# Revit family: VIESSMANN - Vitocal 350-HT Pro
name_source: partatom
category: Wyposażenie mechaniczne
revit_build: Autodesk Revit 2017 (Build: 20160720_1515(x64)
units: mm (PartAtom-declared; Revit-internal decimal feet)

## family parameters
Numer OmniClass = 23.75.10.21.17
Oparty na płaszczyźnie roboczej = Nie
Punkt obliczania pomieszczeń = Nie
Tnij formami wycięć po wczytaniu = Nie
Typ części = Normalny
Tytuł OmniClass = Water-Source Heat Pumps
Współdzielony = Nie
Wymiar okrągłego złącza = Użyj średnicy
Zawsze pionowo = Tak

## types (7) — shared parameters
Autor = www.archispace.pl
Czynnik chłodniczy = R1234ze
Częstotliwość = 50 Hz
Długość strefy serwisowej od przodu = 800 mm  [stored 2.62467 ft]
Liczba biegunów = 3
Maks. cos fi = 1 A
Model = Solankowa pompa ciepła Vitocal 350-HT PRO 80kW / Brine-water heat pump Vitocal 350-HT PRO 80kW
Napięcie znamionowe = 400 V
Obieg pierwotny. Maks. temperatura zasilania na wlocie obiegu pierwotnego = 50 °C
Obieg pierwotny. Min. temperatura zasilania na wlocie obiegu pierwotnego = 0 °C
Odsunięcie strefy serwisowej w szerokości = 456 mm
Opis = Pompy ciepła z napędem elektrycznym do ogrzewania i podgrzewu ciepłej wody użytkowej w jedno- lub dwusystemowych instalacjach grzewczych.
Podłączenie A odsunięcie = 731 mm  [stored 2.39829 ft]
Podłączenie A wysokość = 1365 mm  [stored 4.47835 ft]
Podłączenie C odsunięcie = 311 mm  [stored 1.02034 ft]
Podłączenie C wysokość = 509 mm  [stored 1.66995 ft]
Podłączenie D odsunięcie = 311 mm  [stored 1.02034 ft]
Podłączenie D wysokość = 969 mm  [stored 3.17913 ft]
Podłączenie E odsunięcie = 525 mm
Podłączenie E wysokość = 969 mm  [stored 3.17913 ft]
Podłączenie F odsunięcie = 525 mm
Podłączenie F wysokość = 509 mm  [stored 1.66995 ft]
Podłączenie elektryczne odsunięcie = 797 mm
Podłączenie elektryczne wysokość = 1566 mm
Producent = Viessmann Sp. z o.o.
Stopień ochrony = IP20
Szerokość całkowita = 911 mm  [stored 2.98885 ft]
Szerokość na wlocie = 850 mm  [stored 2.78871 ft]
URL = https://www.viessmann-projektant.pl
Viessmann Kolor 1 = Viessmann Kolor 1
Współczynnik mocy = 1
Wysokość całkowita = 1650 mm  [stored 5.41339 ft]
Zasilanie elektryczne (V/ph/Hz) = 3LNPE/400 V/50 Hz

## per-type parameters (varying)
- BW solanka-woda 2-stopniowy (B0/W35) 352.AHT058: Dopuszczalne ciśnienie robocze. Obieg pierwotny=10 pasek; Dopuszczalne ciśnienie robocze. Obieg wtórny=10 pasek; Dopuszczalne ciśnienie robocze. Strona niskociśnieniowa=19 pasek; Dopuszczalne ciśnienie robocze. Strona wysokociśnieniowa=32 pasek; Długość całkowita=2153 mm  [stored 7.06365 ft]; Ilość oleju=11.0 L; Liczba sprężarek=2; Maks. prąd roboczy=74 A; Masa całkowita (urządzenie podstawowe bez opcjonalnej obudowy)=1077.00 kg; Natężenie znamionowe sprężarek (łącznie)=34 A; Obciążenie pozorne=56600 W; Obieg pierwotny. Minimalny przepływ objętościowy=14.4 m³/h; Obieg pierwotny. Opory przepływu=26.1 pasek; Obieg pierwotny. Pojemność wymiennika ciepła (solanka)=13.0 L; Obieg pierwotny. Znamionowy przepływ objętościowy (wartość zalecana do projektowania)=20.3 m³/h; Obieg wtórny. Maks. temperatura na zasilaniu na wlocie obiegu pierwotnego = 0°=87 °C; Obieg wtórny. Min. temperatura na zasilaniu obiegu wtórnego=24 °C; Obieg wtórny. Minimalny przepływ objętościowy=8.5 m³/h; Obieg wtórny. Opory przepływu=7.7 pasek; Obieg wtórny. Pojemność wymiennika ciepła (woda)=13.0 L; Obieg wtórny. Znamionowy przepływ objętościowy (wartość zalecana do projektowania)=16.6 m³/h; Pobór mocy elektrycznej=13.2 kW; Poziom ciśnienia akustycznego dB(A)=60 mm  [stored 0.19685 ft]; Prąd rozruchowy sprężarki (Part Winding)=Po 125; Prąd rozruchowy sprężarki (łagodny rozruch)=Po 132; SCOP HT=3.11; SCOP LT=3.94; Stopień efektywności ε (COP)=4.3; Typ=Vitocal 350-HT Pro : BW 352.B076, BW 352.B097, BW 352.B114; Wielkość napełnienia (wytyczna)=22.50 kg; Wydajność chłodnicza=43.4 kW; Zabezpieczenie pompy ciepła=125 A; Zasilanie i powrót instalacji grzewczej - przyłącza Victaulic (DN)=65; Zasilanie i powrót obiegu pierwotnego - przyłącza Victaulic (DN)=65; Znamionowa moc grzewcza=56.6 kW; etas HT=117; etas LT=150
- BW solanka-woda 2-stopniowy (B0/W35) 352.AHT071: Dopuszczalne ciśnienie robocze. Obieg pierwotny=32 pasek; Dopuszczalne ciśnienie robocze. Obieg wtórny=19 pasek; Dopuszczalne ciśnienie robocze. Strona niskociśnieniowa=10 pasek; Dopuszczalne ciśnienie robocze. Strona wysokociśnieniowa=10 pasek; Długość całkowita=2153 mm  [stored 7.06365 ft]; Ilość oleju=11.0 L; Liczba sprężarek=2; Maks. prąd roboczy=100 A; Masa całkowita (urządzenie podstawowe bez opcjonalnej obudowy)=1077.00 kg; Natężenie znamionowe sprężarek (łącznie)=49 A; Obciążenie pozorne=72400 W; Obieg pierwotny. Minimalny przepływ objętościowy=14.4 m³/h; Obieg pierwotny. Opory przepływu=0.1 pasek; Obieg pierwotny. Pojemność wymiennika ciepła (solanka)=18.0 L; Obieg pierwotny. Znamionowy przepływ objętościowy (wartość zalecana do projektowania)=17.4 m³/h; Obieg wtórny. Maks. temperatura na zasilaniu na wlocie obiegu pierwotnego = 0°=73 °C; Obieg wtórny. Min. temperatura na zasilaniu obiegu wtórnego=20 °C; Obieg wtórny. Minimalny przepływ objętościowy=8.5 m³/h; Obieg wtórny. Opory przepływu=0.1 pasek; Obieg wtórny. Pojemność wymiennika ciepła (woda)=13.0 L; Obieg wtórny. Znamionowy przepływ objętościowy (wartość zalecana do projektowania)=13.4 m³/h; Pobór mocy elektrycznej=17.0 kW; Poziom ciśnienia akustycznego dB(A)=60 mm  [stored 0.19685 ft]; Prąd rozruchowy sprężarki (Part Winding)=Po 165; Prąd rozruchowy sprężarki (łagodny rozruch)=Po 160; SCOP HT=3.11; SCOP LT=3.94; Stopień efektywności ε (COP)=4.3; Typ=Vitocal 350-HT Pro : BW 352.B076, BW 352.B097, BW 352.B114; Wielkość napełnienia (wytyczna)=30.00 kg; Wydajność chłodnicza=55.4 kW; Zabezpieczenie pompy ciepła=125 A; Zasilanie i powrót instalacji grzewczej - przyłącza Victaulic (DN)=80; Zasilanie i powrót obiegu pierwotnego - przyłącza Victaulic (DN)=80; Znamionowa moc grzewcza=72.4 kW; etas HT=117; etas LT=150
- BW solanka-woda 2-stopniowy (B0/W35) 352.AHT084: Dopuszczalne ciśnienie robocze. Obieg pierwotny=10 pasek; Dopuszczalne ciśnienie robocze. Obieg wtórny=10 pasek; Dopuszczalne ciśnienie robocze. Strona niskociśnieniowa=19 pasek; Dopuszczalne ciśnienie robocze. Strona wysokociśnieniowa=32 pasek; Długość całkowita=2153 mm  [stored 7.06365 ft]; Ilość oleju=11.5 L; Liczba sprężarek=2; Maks. prąd roboczy=115 A; Masa całkowita (urządzenie podstawowe bez opcjonalnej obudowy)=1251.00 kg; Natężenie znamionowe sprężarek (łącznie)=51 A; Obciążenie pozorne=83200 W; Obieg pierwotny. Minimalny przepływ objętościowy=17.3 m³/h; Obieg pierwotny. Opory przepływu=14 pasek; Obieg pierwotny. Pojemność wymiennika ciepła (solanka)=22.0 L; Obieg pierwotny. Znamionowy przepływ objętościowy (wartość zalecana do projektowania)=20.0 m³/h; Obieg wtórny. Maks. temperatura na zasilaniu na wlocie obiegu pierwotnego = 0°=73 °C; Obieg wtórny. Min. temperatura na zasilaniu obiegu wtórnego=20 °C; Obieg wtórny. Minimalny przepływ objętościowy=10.0 m³/h; Obieg wtórny. Opory przepływu=13 pasek; Obieg wtórny. Pojemność wymiennika ciepła (woda)=15.0 L; Obieg wtórny. Znamionowy przepływ objętościowy (wartość zalecana do projektowania)=14.4 m³/h; Pobór mocy elektrycznej=19.6 kW; Poziom ciśnienia akustycznego dB(A)=65 mm  [stored 0.213255 ft]; Prąd rozruchowy sprężarki (Part Winding)=Po 165; Prąd rozruchowy sprężarki (łagodny rozruch)=Po 193; SCOP HT=3.21; SCOP LT=3.92; Stopień efektywności ε (COP)=4.2; Typ=Vitocal 350-HT Pro : BW 352.B076, BW 352.B097, BW 352.B114; Wielkość napełnienia (wytyczna)=36.00 kg; Wydajność chłodnicza=63.6 kW; Zabezpieczenie pompy ciepła=160 A; Zasilanie i powrót instalacji grzewczej - przyłącza Victaulic (DN)=80; Zasilanie i powrót obiegu pierwotnego - przyłącza Victaulic (DN)=80; Znamionowa moc grzewcza=83.2 kW; etas HT=120; etas LT=149
- BW solanka-woda 2-stopniowy (B0/W35) 352.AHT096: Dopuszczalne ciśnienie robocze. Obieg pierwotny=10 pasek; Dopuszczalne ciśnienie robocze. Obieg wtórny=10 pasek; Dopuszczalne ciśnienie robocze. Strona niskociśnieniowa=19 pasek; Dopuszczalne ciśnienie robocze. Strona wysokociśnieniowa=32 pasek; Długość całkowita=2153 mm  [stored 7.06365 ft]; Ilość oleju=11.5 L; Liczba sprężarek=2; Maks. prąd roboczy=136 A; Masa całkowita (urządzenie podstawowe bez opcjonalnej obudowy)=1357.00 kg; Natężenie znamionowe sprężarek (łącznie)=67 A; Obciążenie pozorne=96600 W; Obieg pierwotny. Minimalny przepływ objętościowy=15.4 m³/h; Obieg pierwotny. Opory przepływu=15 pasek; Obieg pierwotny. Pojemność wymiennika ciepła (solanka)=33.0 L; Obieg pierwotny. Znamionowy przepływ objętościowy (wartość zalecana do projektowania)=23.1 m³/h; Obieg wtórny. Maks. temperatura na zasilaniu na wlocie obiegu pierwotnego = 0°=73 °C; Obieg wtórny. Min. temperatura na zasilaniu obiegu wtórnego=20 °C; Obieg wtórny. Minimalny przepływ objętościowy=11.0 m³/h; Obieg wtórny. Opory przepływu=14 pasek; Obieg wtórny. Pojemność wymiennika ciepła (woda)=17.0 L; Obieg wtórny. Znamionowy przepływ objętościowy (wartość zalecana do projektowania)=16.7 m³/h; Pobór mocy elektrycznej=23.2 kW; Poziom ciśnienia akustycznego dB(A)=65 mm  [stored 0.213255 ft]; Prąd rozruchowy sprężarki (Part Winding)=Po 219; Prąd rozruchowy sprężarki (łagodny rozruch)=Po 222; SCOP HT=3.11; SCOP LT=3.86; Stopień efektywności ε (COP)=4.2; Typ=Vitocal 350-HT Pro : BW 352.B076, BW 352.B097, BW 352.B114; Wielkość napełnienia (wytyczna)=42.00 kg; Wydajność chłodnicza=73.4 kW; Zabezpieczenie pompy ciepła=160 A; Zasilanie i powrót instalacji grzewczej - przyłącza Victaulic (DN)=80; Zasilanie i powrót obiegu pierwotnego - przyłącza Victaulic (DN)=80; Znamionowa moc grzewcza=96.6 kW; etas HT=116; etas LT=146
- BW solanka-woda 2-stopniowy (B0/W35) 352.AHT119: Dopuszczalne ciśnienie robocze. Obieg pierwotny=10 pasek; Dopuszczalne ciśnienie robocze. Obieg wtórny=10 pasek; Dopuszczalne ciśnienie robocze. Strona niskociśnieniowa=19 pasek; Dopuszczalne ciśnienie robocze. Strona wysokociśnieniowa=32 pasek; Długość całkowita=2153 mm  [stored 7.06365 ft]; Ilość oleju=11.5 L; Liczba sprężarek=2; Maks. prąd roboczy=166 A; Masa całkowita (urządzenie podstawowe bez opcjonalnej obudowy)=1426.00 kg; Natężenie znamionowe sprężarek (łącznie)=91 A; Obciążenie pozorne=116800 W; Obieg pierwotny. Minimalny przepływ objętościowy=17.3 m³/h; Obieg pierwotny. Opory przepływu=16 pasek; Obieg pierwotny. Pojemność wymiennika ciepła (solanka)=39.0 L; Obieg pierwotny. Znamionowy przepływ objętościowy (wartość zalecana do projektowania)=27.8 m³/h; Obieg wtórny. Maks. temperatura na zasilaniu na wlocie obiegu pierwotnego = 0°=73 °C; Obieg wtórny. Min. temperatura na zasilaniu obiegu wtórnego=20 °C; Obieg wtórny. Minimalny przepływ objętościowy=13.0 m³/h; Obieg wtórny. Opory przepływu=17 pasek; Obieg wtórny. Pojemność wymiennika ciepła (woda)=20.0 L; Obieg wtórny. Znamionowy przepływ objętościowy (wartość zalecana do projektowania)=20.2 m³/h; Pobór mocy elektrycznej=28.4 kW; Poziom ciśnienia akustycznego dB(A)=65 mm  [stored 0.213255 ft]; Prąd rozruchowy sprężarki (Part Winding)=Po 226; Prąd rozruchowy sprężarki (łagodny rozruch)=Po 252; SCOP HT=3.07; SCOP LT=3.82; Stopień efektywności ε (COP)=4.1; Typ=Vitocal 350-HT Pro : BW 352.B076, BW 352.B097, BW 352.B114; Wielkość napełnienia (wytyczna)=49.50 kg; Wydajność chłodnicza=88.4 kW; Zabezpieczenie pompy ciepła=200 A; Zasilanie i powrót instalacji grzewczej - przyłącza Victaulic (DN)=80; Zasilanie i powrót obiegu pierwotnego - przyłącza Victaulic (DN)=80; Znamionowa moc grzewcza=116.8 kW; etas HT=115; etas LT=145
- BW solanka-woda 3-stopniowy (B0/W35) 352.AHT126: Dopuszczalne ciśnienie robocze. Obieg pierwotny=10 pasek; Dopuszczalne ciśnienie robocze. Obieg wtórny=10 pasek; Dopuszczalne ciśnienie robocze. Strona niskociśnieniowa=19 pasek; Dopuszczalne ciśnienie robocze. Strona wysokociśnieniowa=32 pasek; Długość całkowita=2816 mm  [stored 9.23885 ft]; Ilość oleju=16.3 L; Liczba sprężarek=3; Maks. prąd roboczy=173 A; Masa całkowita (urządzenie podstawowe bez opcjonalnej obudowy)=1779.00 kg; Natężenie znamionowe sprężarek (łącznie)=77 A; Obciążenie pozorne=124800 W; Obieg pierwotny. Minimalny przepływ objętościowy=19.2 m³/h; Obieg pierwotny. Opory przepływu=15 pasek; Obieg pierwotny. Pojemność wymiennika ciepła (solanka)=42.0 L; Obieg pierwotny. Znamionowy przepływ objętościowy (wartość zalecana do projektowania)=30.0 m³/h; Obieg wtórny. Maks. temperatura na zasilaniu na wlocie obiegu pierwotnego = 0°=73 °C; Obieg wtórny. Min. temperatura na zasilaniu obiegu wtórnego=20 °C; Obieg wtórny. Minimalny przepływ objętościowy=15.5 m³/h; Obieg wtórny. Opory przepływu=16 pasek; Obieg wtórny. Pojemność wymiennika ciepła (woda)=23.0 L; Obieg wtórny. Znamionowy przepływ objętościowy (wartość zalecana do projektowania)=21.6 m³/h; Pobór mocy elektrycznej=29.4 kW; Poziom ciśnienia akustycznego dB(A)=65 mm  [stored 0.213255 ft]; Prąd rozruchowy sprężarki (Part Winding)=Po 165; Prąd rozruchowy sprężarki (łagodny rozruch)=Po 193; SCOP HT=3.14; SCOP LT=3.92; Stopień efektywności ε (COP)=4.2; Typ=Vitocal 350-HT Pro : BW 353.B172, BW 353.B198; Wielkość napełnienia (wytyczna)=57.00 kg; Wydajność chłodnicza=95.4 kW; Zabezpieczenie pompy ciepła=200 A; Zasilanie i powrót instalacji grzewczej - przyłącza Victaulic (DN)=80; Zasilanie i powrót obiegu pierwotnego - przyłącza Victaulic (DN)=80; Znamionowa moc grzewcza=124.8 kW; etas HT=118; etas LT=149
- BW solanka-woda 3-stopniowy (B0/W35) 352.AHT147: Dopuszczalne ciśnienie robocze. Obieg pierwotny=10 pasek; Dopuszczalne ciśnienie robocze. Obieg wtórny=10 pasek; Dopuszczalne ciśnienie robocze. Strona niskociśnieniowa=19 pasek; Dopuszczalne ciśnienie robocze. Strona wysokociśnieniowa=32 pasek; Długość całkowita=2816 mm  [stored 9.23885 ft]; Ilość oleju=16.3 L; Liczba sprężarek=3; Maks. prąd roboczy=203 A; Masa całkowita (urządzenie podstawowe bez opcjonalnej obudowy)=1865.00 kg; Natężenie znamionowe sprężarek (łącznie)=100 A; Obciążenie pozorne=144900 W; Obieg pierwotny. Minimalny przepływ objętościowy=22.0 m³/h; Obieg pierwotny. Opory przepływu=15 pasek; Obieg pierwotny. Pojemność wymiennika ciepła (solanka)=50.0 L; Obieg pierwotny. Znamionowy przepływ objętościowy (wartość zalecana do projektowania)=34.6 m³/h; Obieg wtórny. Maks. temperatura na zasilaniu na wlocie obiegu pierwotnego = 0°=73 °C; Obieg wtórny. Min. temperatura na zasilaniu obiegu wtórnego=20 °C; Obieg wtórny. Minimalny przepływ objętościowy=18.0 m³/h; Obieg wtórny. Opory przepływu=18 pasek; Obieg wtórny. Pojemność wymiennika ciepła (woda)=28.0 L; Obieg wtórny. Znamionowy przepływ objętościowy (wartość zalecana do projektowania)=25.1 m³/h; Pobór mocy elektrycznej=34.8 kW; Poziom ciśnienia akustycznego dB(A)=65 mm  [stored 0.213255 ft]; Prąd rozruchowy sprężarki (Part Winding)=Po 219; Prąd rozruchowy sprężarki (łagodny rozruch)=Po 222; SCOP HT=3.11; SCOP LT=3.86; Stopień efektywności ε (COP)=4.2; Typ=Vitocal 350-HT Pro : BW 353.B172, BW 353.B198; Wielkość napełnienia (wytyczna)=68.00 kg; Wydajność chłodnicza=110.1 kW; Zabezpieczenie pompy ciepła=250 A; Zasilanie i powrót instalacji grzewczej - przyłącza Victaulic (DN)=80; Zasilanie i powrót obiegu pierwotnego - przyłącza Victaulic (DN)=80; Znamionowa moc grzewcza=144.9 kW; etas HT=117; etas LT=146

note: [stored X ft] marks values corroborated as IEEE doubles in the binary element streams (Revit-internal decimal feet)

## geometry (parser evidence)
native form markers: Sweep x3
no freeform markers — native parametric forms only
